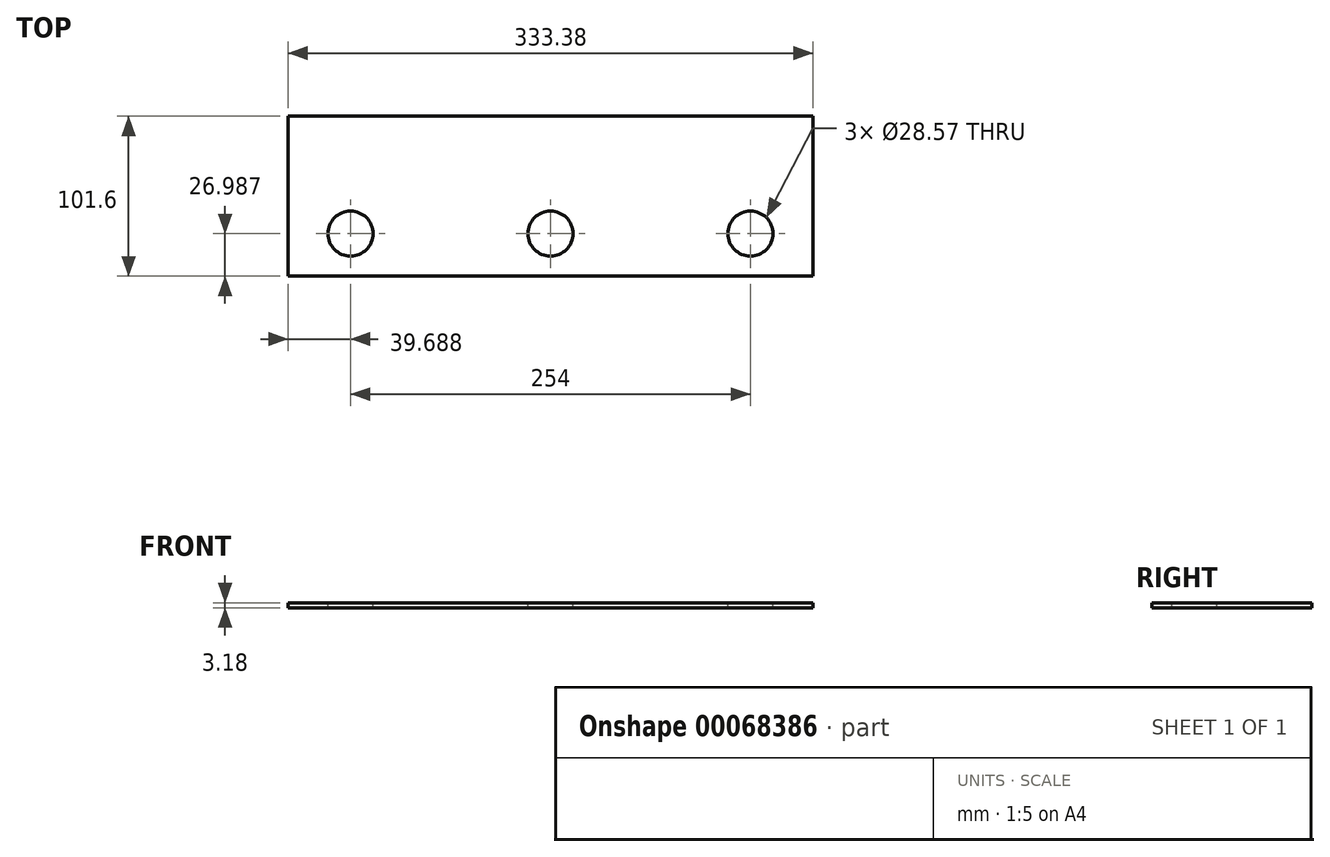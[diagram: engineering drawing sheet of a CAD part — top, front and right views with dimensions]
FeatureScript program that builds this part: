
annotation { "Feature Type Name" : "Feature", "Feature Type Description" : "" }
export const myFeature = defineFeature(function(context is Context, id is Id, definition is map)
    precondition{}
    {
        {
            var Q0;
            Q0=qCreatedBy(makeId("Top.planeOp"),FACE);
            var sketch = newSketch(context, id + "F0", { "sketchPlane" : qUnion([Q0])});
            skLineSegment(sketch, "E0.bottom", {"start": v(0, 0) * mm, "end": v(333.38, 0) * mm});
            skLineSegment(sketch, "E0.top", {"start": v(0, -101.6) * mm, "end": v(333.38, -101.6) * mm});
            skLineSegment(sketch, "E0.left", {"start": v(0, 0) * mm, "end": v(0, -101.6) * mm});
            skLineSegment(sketch, "E0.right", {"start": v(333.38, 0) * mm, "end": v(333.38, -101.6) * mm});
            skSolve(sketch);
        }
        {
            var Q0;
            Q0 = qSketchRegion(id + "F0", true);
            extrude(context, id + "F1", {"entities" : qUnion([Q0]), "depth" : 3.17 * mm});
        }
        {
            var Q0;
            Q0=makeQuery(id+"F1.opExtrude","CAP_FACE",FACE,{"disambiguationData":[OSD([sQuery(id+"F0.wireOp",EDGE,"E0.bottom"),sQuery(id+"F0.wireOp",EDGE,"E0.top"),sQuery(id+"F0.wireOp",EDGE,"E0.left"),sQuery(id+"F0.wireOp",EDGE,"E0.right")])],"isStart":false});
            var sketch = newSketch(context, id + "F2", { "sketchPlane" : qUnion([Q0])});
            skCircle(sketch, "E1", {"center": v(39.69, -74.61) * mm, "radius": 14.29 * mm});
            skCircle(sketch, "E2", {"center": v(166.69, -74.61) * mm, "radius": 14.29 * mm});
            skCircle(sketch, "E3", {"center": v(293.69, -74.61) * mm, "radius": 14.29 * mm});
            skSolve(sketch);
        }
        {
            var Q0;
            Q0 = qSketchRegion(id + "F2", true);
            extrude(context, id + "F3", {"entities" : qUnion([Q0]), "operationType" : NewBodyOperationType.REMOVE, "oppositeDirection" : true, "depth" : 25.4 * mm});
        }
    });
